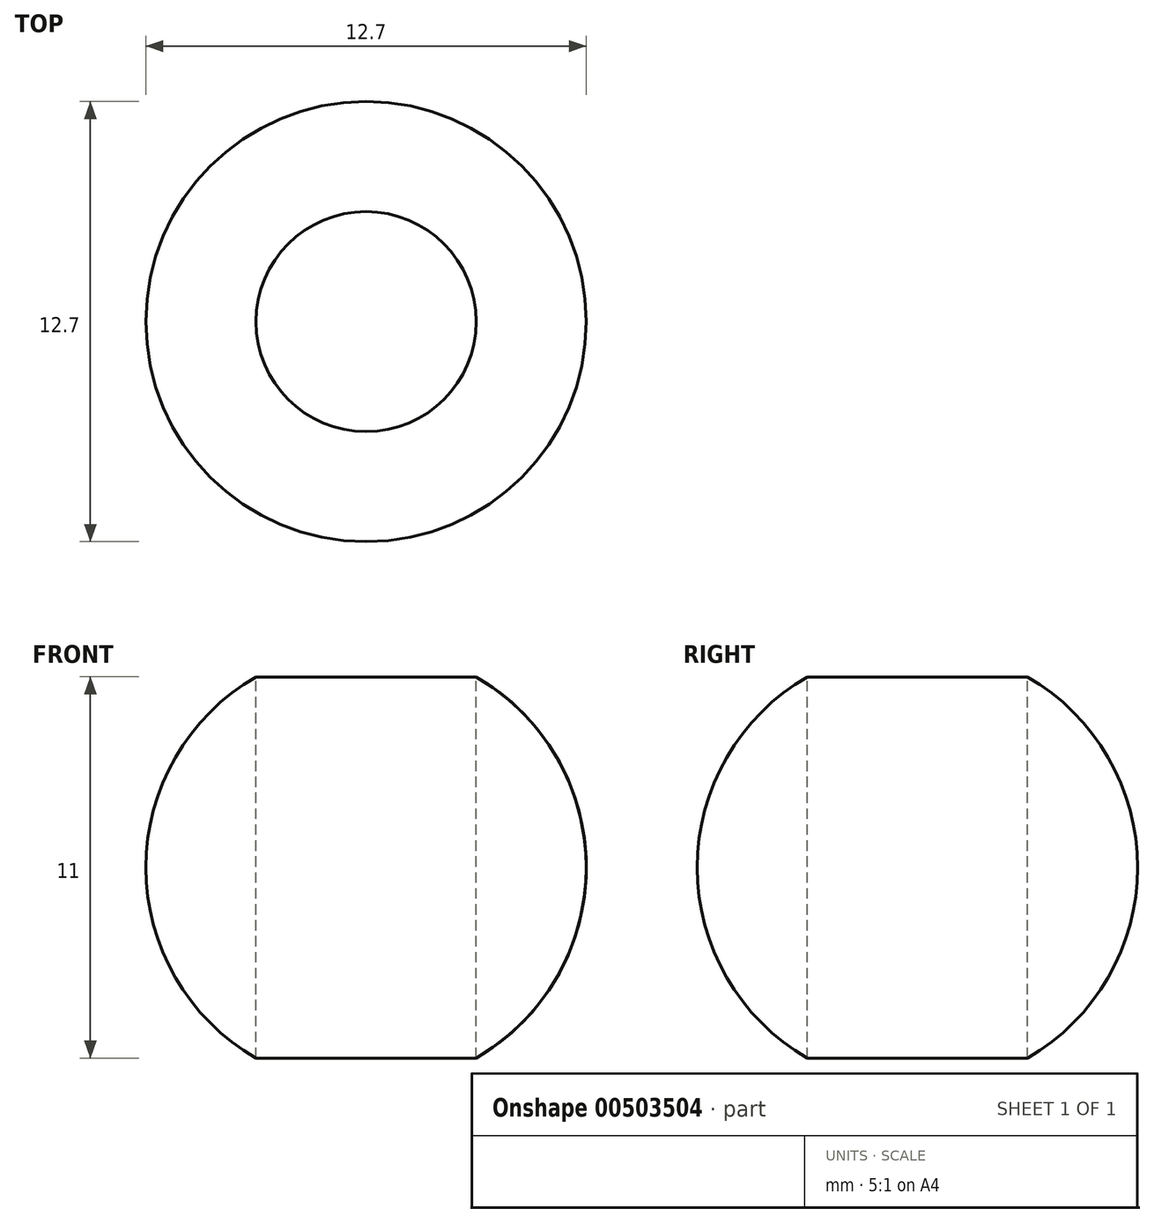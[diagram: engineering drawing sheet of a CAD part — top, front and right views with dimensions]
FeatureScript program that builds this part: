
annotation { "Feature Type Name" : "Feature", "Feature Type Description" : "" }
export const myFeature = defineFeature(function(context is Context, id is Id, definition is map)
    precondition{}
    {
        {
            var Q0;
            Q0=qCreatedBy(makeId("Front.planeOp"),FACE);
            var sketch = newSketch(context, id + "F0", { "sketchPlane" : qUnion([Q0])});
            skLineSegment(sketch, "E0", {"start": v(3.17, 5.5) * mm, "end": v(3.18, -5.5) * mm});
            skPoint(sketch, "E1", {"position": v(3.17, 0) * mm});
            skArc(sketch, "E2", {"start": v(3.18, 5.5) * mm, "mid": v(6.35, 0) * mm, "end": v(3.18, -5.5) * mm});
            skLineSegment(sketch, "E3", {"start": v(0, 5.5) * mm, "end": v(0, -5.5) * mm, "construction": true});
            skSolve(sketch);
        }
        {
            var Q0;
            Q0=makeQuery(id+"F0.imprint","IMPRINT",FACE,{"disambiguationData":[TD([[makeQuery(id+"F0.imprint","IMPRINT",EDGE,{"derivedFrom":sQuery(id+"F0.wireOp",EDGE,"E0")}),1.0]])]});
            var Q1;
            Q1=sQuery(id+"F0.wireOp",EDGE,"E3");
            revolve(context, id + "F1", {"entities" : qUnion([Q0]), "axis" : qUnion([Q1]), "revolveType" : RevolveType.FULL});
        }
        {
            var Q0;
            Q0=qCreatedBy(makeId("Top.planeOp"),FACE);
            var sketch = newSketch(context, id + "F2", { "sketchPlane" : qUnion([Q0])});
            skLineSegment(sketch, "E4.bottom", {"start": v(7.94, 7.94) * mm, "end": v(-7.94, 7.94) * mm});
            skLineSegment(sketch, "E4.top", {"start": v(7.94, -7.94) * mm, "end": v(-7.94, -7.94) * mm});
            skLineSegment(sketch, "E4.left", {"start": v(7.94, 7.94) * mm, "end": v(7.94, -7.94) * mm});
            skLineSegment(sketch, "E4.right", {"start": v(-7.94, 7.94) * mm, "end": v(-7.94, -7.94) * mm});
            skPoint(sketch, "E4.middle", {"position": v(0, 0) * mm});
            skSolve(sketch);
        }
        {
            var Q0;
            Q0=makeQuery(id+"F2.imprint","IMPRINT",FACE,{"disambiguationData":[TD([[makeQuery(id+"F2.imprint","IMPRINT",EDGE,{"derivedFrom":sQuery(id+"F2.wireOp",EDGE,"E4.bottom")}),1.0]])]});
            extrude(context, id + "F3", {"entities" : qUnion([Q0]), "endBound" : BoundingType.SYMMETRIC, "depth" : 1 / 101.6 * mm});
        }
        {
            var Q0;
            Q0=makeQuery(id+"F1.opRevolve","SWEPT_BODY",BODY,{"disambiguationData":[OSD([sQuery(id+"F0.wireOp",EDGE,"E0"),sQuery(id+"F0.wireOp",EDGE,"E2")])]});
            var Q1;
            Q1=makeQuery(id+"F3.opExtrude","SWEPT_BODY",BODY,{"disambiguationData":[OSD([sQuery(id+"F2.wireOp",EDGE,"E4.bottom"),sQuery(id+"F2.wireOp",EDGE,"E4.top"),sQuery(id+"F2.wireOp",EDGE,"E4.left"),sQuery(id+"F2.wireOp",EDGE,"E4.right")])]});
            booleanBodies(context, id + "F4", {"operationType" : BooleanOperationType.SUBTRACTION, "tools" : qUnion([Q0]), "targets" : qUnion([Q1]), "keepTools" : true});
        }
        {
            var Q0;
            Q0=makeQuery(id+"F4.opBoolean","SPLIT",BODY,{"disambiguationData":[OD(1.0)],"derivedFrom":makeQuery(id+"F3.opExtrude","SWEPT_BODY",BODY,{"disambiguationData":[OSD([sQuery(id+"F2.wireOp",EDGE,"E4.bottom"),sQuery(id+"F2.wireOp",EDGE,"E4.top"),sQuery(id+"F2.wireOp",EDGE,"E4.left"),sQuery(id+"F2.wireOp",EDGE,"E4.right")])]})});
            deleteBodies(context, id + "F5", {"entities" : qUnion([Q0])});
        }
    });
